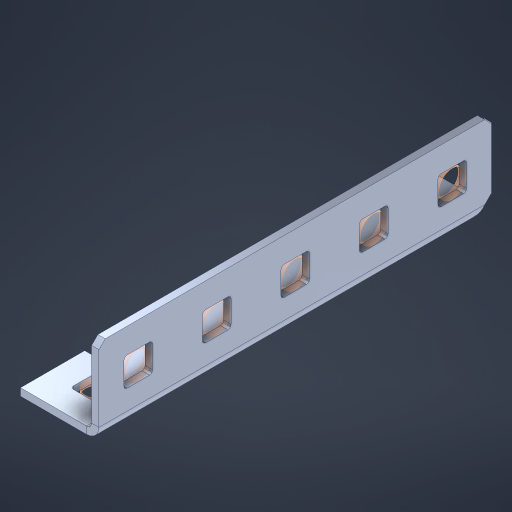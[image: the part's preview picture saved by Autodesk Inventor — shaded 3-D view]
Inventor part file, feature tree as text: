
AUTODESK INVENTOR PART (.ipt)
format: ipt  version: 2023 (Build 270158000, 158)  size: 556,032 bytes
history: native  units: in
note: dims shown in document units (in); Inventor stores cm internally (conversion verified against a paired STEP export)
features: other x22, extrude x13, sheet_metal_op x11, sketch x10, pattern_linear x2, mirror x1, chamfer x1
ambient origin geometry x8: Origin, YZ Plane, XZ Plane, XY Plane, X Axis, Y Axis, Z Axis, Center Point
bodies: Solid1 (feature_tree), Body (feature_tree)
feature tree (60):
  sheet_metal_op  "Flanges"
  other  "Flange Pattern Plane"
  other  "Flange Pattern Sketch"
  sheet_metal_op  "Flange Pattern"
  sheet_metal_op  "Body Pattern"
  pattern_linear  "Center Pattern"  Spacing1=0.0469in  [1 undecoded]
  other  "Arc Length"
  mirror  "Notch Mirror"
  pattern_linear  "Notch Pattern"  Spacing1=0.182in  [1 undecoded]
  chamfer  "End Chamfer"
  extrude  "Half Cut"  Depth=0.02in
  sketch  "Sketch1"  dims[d0=1.0in]
  other  "Plate1"
  sketch  "Sketch2"  dims[d1=2.5in]
  other  "Plate2"
  sheet_metal_op  "Bend1"
  sheet_metal_op  "Corner1"
  sketch  "Sketch3"  dims[d2=0.0469in]
  sketch  "Sketch7"  dims[d3=0.0469in]
  other  "Srf1"
  other  "Srf2"
  sketch  "Sketch8"  dims[d4=0.0234in]
  sketch  "Sketch9"  dims[d5=0.0938in]
  other  "Srf91"
  sheet_metal_op  "Body Pattern Sketch"
  other  "Srf92"
  sketch  "Sketch13"  dims[d6=0.0469in]
  sketch  "Sketch14"  dims[d7=0.5in d8=90.0deg d9=0.0312in]
  sketch  "Sketch15"  dims[d10=0.1875in]
  sketch  "Sketch16"  dims[d11=0.0469in d12=0.0469in d16=0.182in d17=0.02in d18=0.0469in d19=0.0in d20=0.25in d21=0.25in d38=1.9685in d40=0.5in d41=0.3937in d43=1.0in d46=0.172in d47=1.0in d48=0.0in d49=0.182in d50=0.02in d51=0.25in d52=0.25in d53=0.0469in d54=0.0in d55=0.172in d56=1.0in d57=0.0in d58=0.25in d60=1.9685in d62=0.5in d63=0.3937in d65=0.5in d85=0.1227in d86=0.1659in d88=0.04in d89=0.0469in d90=0.0in d91=0.04in d92=0.0491in d95=2.5in d96=0.04in d97=0.25in d98=45.0deg d99=0.25in d100=0.5in d101=0.0in d102=2.497in d106=0.182in d107=0.02in d108=0.5in d109=0.5in d110=0.0469in d111=0.0in d112=0.172in d113=0.5in d114=0.0in d117=0.5in d118=0.5in d119=0.5in]
  other  "Srf786"
  other  "Srf823"
  other  "Srf824"
  other  "Srf825"
  other  "Srf856"
  other  "Srf857"
  other  "Srf858"
  other  "Srf889"
  other  "Srf890"
  other  "Srf891"
  other  "Srf892"
  sheet_metal_op  "Flange Stamp"
  sheet_metal_op  "Flange Circle"
  sheet_metal_op  "Body Stamp"
  sheet_metal_op  "Body Circle"
  other  "Center Stamp"
  other  "Center Circle"
  sheet_metal_op  "Notch"
  extrude  "ExtrusionSrf2"  Depth=0.0469in
  extrude  "ExtrusionSrf92"  TaperAngle=0.0deg  [1 undecoded]
  extrude  "ExtrusionSrf823"  Depth=0.25in
  extrude  "ExtrusionSrf824"  Depth=0.25in
  extrude  "ExtrusionSrf825"  Depth=0.5in
  extrude  "ExtrusionSrf856"  Depth=0.5in
  extrude  "ExtrusionSrf857"  Depth=1.0in TaperAngle=0.0deg
  extrude  "ExtrusionSrf858"  Depth=0.182in
  extrude  "ExtrusionSrf889"  Depth=0.02in
  extrude  "ExtrusionSrf890"  Depth=0.25in
  extrude  "ExtrusionSrf891"  Depth=0.25in
  extrude  "ExtrusionSrf892"  Depth=0.0469in
note: 3 required parameter values undecoded (feature->parameter linkage not recoverable at this tier; creation-order binding heuristic only, values carry confidence <= 0.55)
